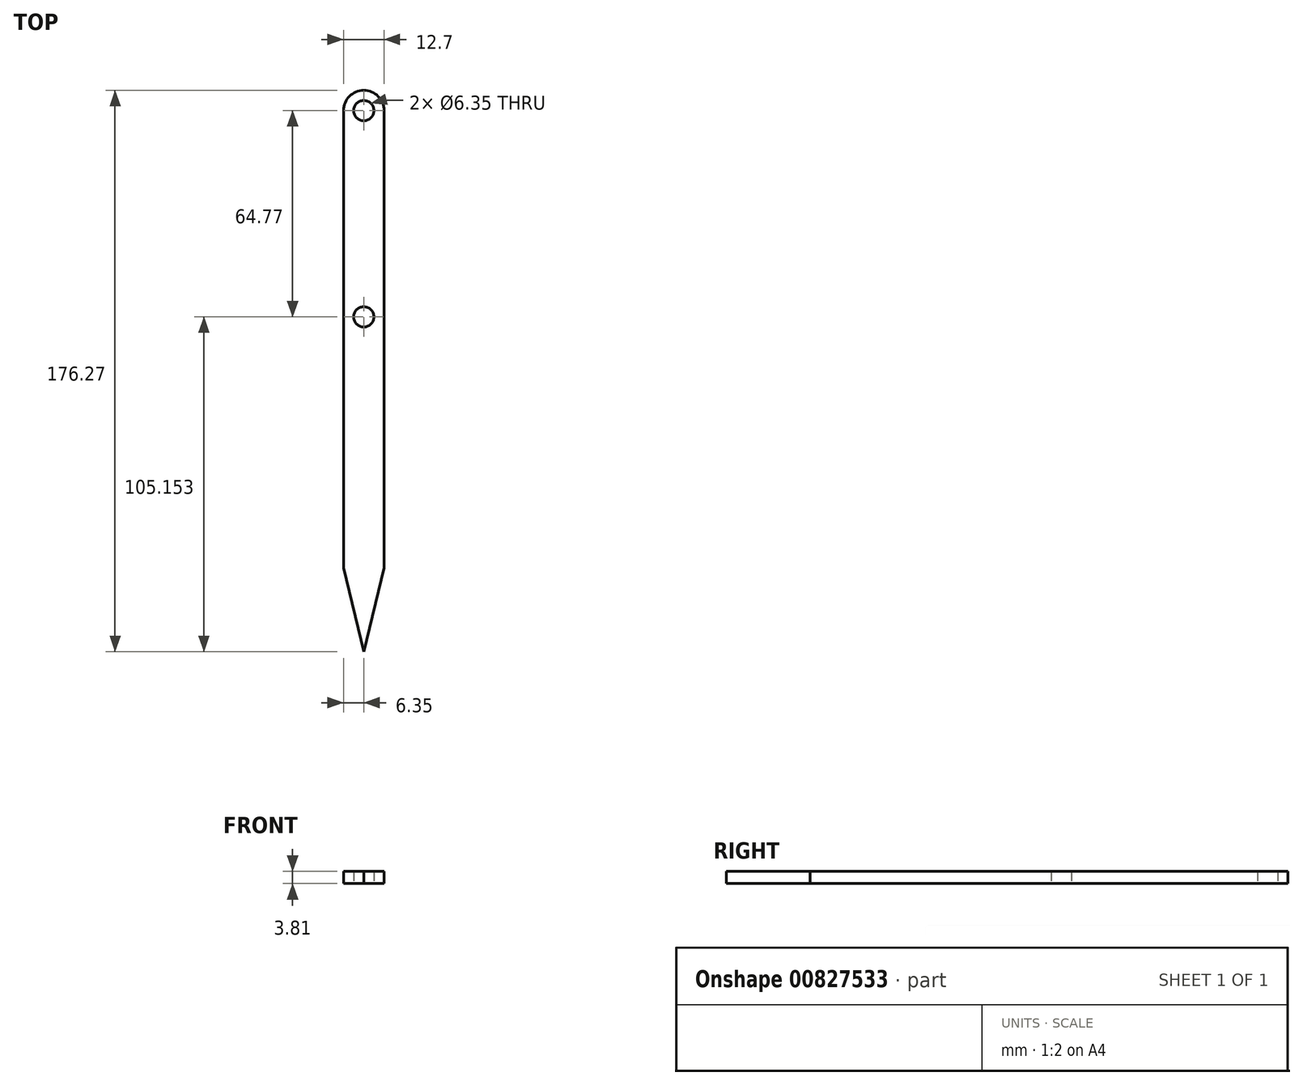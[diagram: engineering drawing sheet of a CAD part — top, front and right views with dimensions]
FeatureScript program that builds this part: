
annotation { "Feature Type Name" : "Feature", "Feature Type Description" : "" }
export const myFeature = defineFeature(function(context is Context, id is Id, definition is map)
    precondition{}
    {
        {
            var Q0;
            Q0=qCreatedBy(makeId("Top.planeOp"),FACE);
            var sketch = newSketch(context, id + "F0", { "sketchPlane" : qUnion([Q0])});
            skLineSegment(sketch, "E0.bottom", {"start": v(-6.35, 84.96) * mm, "end": v(6.35, 84.96) * mm});
            skLineSegment(sketch, "E0.top", {"start": v(-6.35, -84.96) * mm, "end": v(6.35, -84.96) * mm});
            skLineSegment(sketch, "E0.left", {"start": v(-6.35, 84.96) * mm, "end": v(-6.35, -84.96) * mm});
            skLineSegment(sketch, "E0.right", {"start": v(6.35, 84.96) * mm, "end": v(6.35, -84.96) * mm});
            skPoint(sketch, "E0.middle", {"position": v(0, 0) * mm});
            skLineSegment(sketch, "E1", {"start": v(0, -84.96) * mm, "end": v(-6.35, -58.62) * mm});
            skLineSegment(sketch, "E2", {"start": v(-6.35, -58.62) * mm, "end": v(6.35, -58.62) * mm});
            skLineSegment(sketch, "E3", {"start": v(6.35, -58.62) * mm, "end": v(0, -84.96) * mm});
            skCircle(sketch, "E4", {"center": v(0, 84.96) * mm, "radius": 3.18 * mm});
            skArc(sketch, "E5", {"start": v(6.35, 84.96) * mm, "mid": v(0, 91.31) * mm, "end": v(-6.35, 84.96) * mm});
            skCircle(sketch, "E6", {"center": v(0, 20.2) * mm, "radius": 3.18 * mm});
            skSolve(sketch);
        }
        {
            var Q0;
            {var subQ4=sQuery(id+"F0.wireOp",EDGE,"E2");Q0=makeQuery(id+"F0.imprint","IMPRINT",FACE,{"disambiguationData":[TD([[makeQuery(id+"F0.imprint","IMPRINT",EDGE,{"derivedFrom":subQ4}),1.0]])]});}
            var Q1;
            Q1=makeQuery(id+"F0.imprint","IMPRINT",FACE,{"disambiguationData":[TD([[makeQuery(id+"F0.imprint","IMPRINT",EDGE,{"derivedFrom":sQuery(id+"F0.wireOp",EDGE,"E1")}),-1.0]])]});
            var Q2;
            {var subQ0=sQuery(id+"F0.wireOp",EDGE,"E5");Q2=makeQuery(id+"F0.imprint","IMPRINT",FACE,{"disambiguationData":[TD([[makeQuery(id+"F0.imprint","IMPRINT",EDGE,{"derivedFrom":subQ0}),1.0]])]});}
            extrude(context, id + "F1", {"entities" : qUnion([Q0, Q1, Q2]), "depth" : 3.8 * mm, "offsetDistance" : 25.4 * mm});
        }
    });
